# Revit family: Cameo 1.7
name_source: partatom
category: Lighting Fixtures
revit_build: Autodesk Revit 2017 (Build: 20170419_0315(x64)
units: mm (PartAtom-declared; Revit-internal decimal feet)

## family parameters
Cut with Voids When Loaded = Yes
Host = Face
Light Source = No
Part Type = Normal
Room Calculation Point = Yes
Round Connector Dimension = Use Diameter
Shared = No

## types (5) — shared parameters
Apparent Load Phase 1 = 3 W
Body = L&L_White anodized aluminium
CRI = 90
Code = CM1700100050SN Black; CM1700100050SE White
Control system = -
Cutout dimensions = diam. 54 mm
Default Elevation = 1219 mm
Delivered lumen output = 144 lm (3000K, 29°)
Energy efficiency class = A A+ A++
Features = -
Frame = L&L_Black anodized
Geometry 1 = Cameo1.7_fixed
Geometry 2 = Cameo1.7_mod : Cameo 1.7
Geometry 3 = Cameo1.7_frame
Height mm = 28 mm
Height void = 30 mm  [stored 0.0984252 ft]
Horizontal rotation max = 360.00°
IP = 40
L1 = 11 mm
LED Colour = 3000K (also available: 2700K and 4000K - ref. URL Technical sheet)
Length mm = 58 mm  [stored 0.190289 ft]
Lens = L&L_Tempered extra-clear glass
Lumen output at source = 157 lm (3000K)
Manufacturer = L&L Luce&Light
Material = body and trim in aluminium
Model = Cameo 1.7
Mounting = recessed (ceilings, and false ceilings and niches in plasterboard)
No. and type of led = 1 power LED, 1/4 ANSI BIN, 50 000h L90 B10 (Ta 25°C)
Notes = The light beam can be precisely directed thanks to the great adjustability of the optical unit: rotation up to 360° around the vertical axis and 20° along the horizontal axis
Power = 2.5W
Power cables = includes 1.5 m PVC cable FROR 2x0.35/0.35 Ø3.5 m
Power supply = 24Vdc
Power supply unit = not included
Radius void = 25 mm  [stored 0.082021 ft]
Springs = L&L_C 67 annealed steel
URL = https://www.lucelight.it
URL Accessories and power supply units = https://www.lucelight.it
URL Catalogue = -
URL DXF = https://www.lucelight.it
URL Description = https://www.lucelight.it
URL General code = https://www.lucelight.it
URL IES Photometric file = https://www.lucelight.it
URL Image = https://www.lucelight.it
URL Technical sheet = https://www.lucelight.it
Vertical Rotation max = 20.00°
Vertical rotation max = 20.00°
Vertical rotation min = -20.00°
Voltage = 24 V
Weight kg = 0.07 kg
Width mm = 58 mm  [stored 0.190289 ft]
Wiring = parallel

## per-type parameters (varying)
| type | Description | Light Source | Optics |
| Cameo 1.7_L 52° (3000K 2.5W 24Vdc) | Recessed for indoor applications | Light Source : L52° | 52° |
| Cameo 1.7_M 29° (3000K 2.5W 24Vdc) | indoor recessed | Light Source : M29° | 29° |
| Cameo 1.7_P 48° (3000K 2.5W 24Vdc) | indoor recessed | Light Source : P48° | 48° |
| Cameo 1.7_S 17° (3000K 2.5W 24Vdc) | indoor recessed | Light Source : S17° | 17° |
| Cameo 1.7_W 16°x34° (3000K 2.5W 24Vdc) | indoor recessed | Light Source : W16°x34° | 16°x34° |

note: [stored X ft] marks values corroborated as IEEE doubles in the binary element streams (Revit-internal decimal feet)

## geometry (parser evidence)
native form markers: Blend x2, Sweep x17
no freeform markers — native parametric forms only
